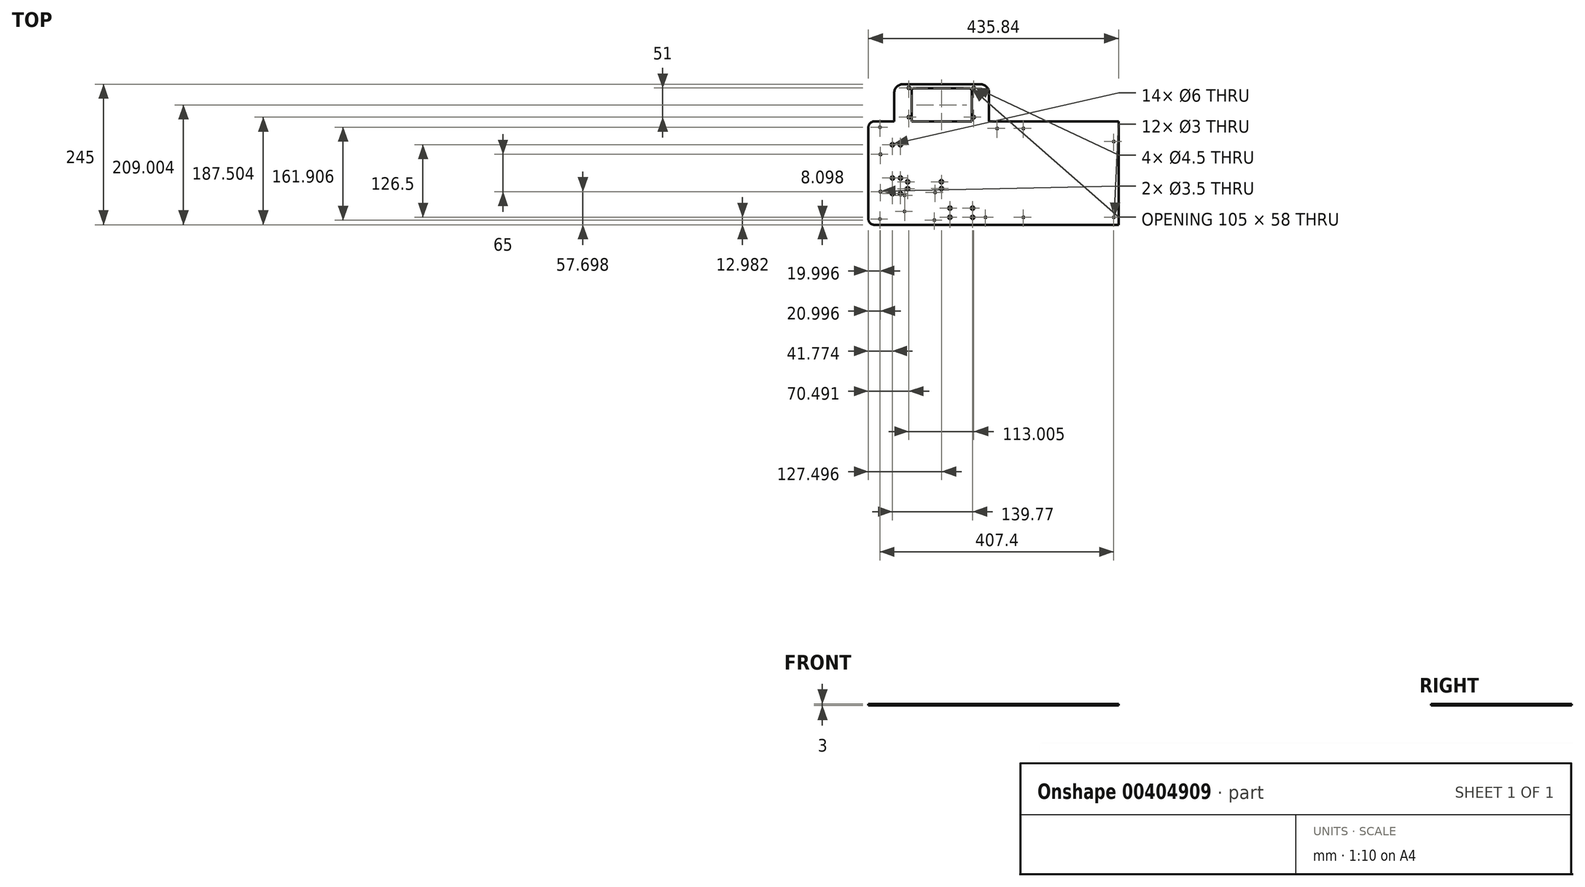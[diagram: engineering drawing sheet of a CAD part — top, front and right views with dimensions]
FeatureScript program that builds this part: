
annotation { "Feature Type Name" : "Feature", "Feature Type Description" : "" }
export const myFeature = defineFeature(function(context is Context, id is Id, definition is map)
    precondition{}
    {
        {
            var Q0;
            Q0=qCreatedBy(makeId("Top.planeOp"),FACE);
            var sketch = newSketch(context, id + "F0", { "sketchPlane" : qUnion([Q0])});
            skLineSegment(sketch, "E0.bottom", {"start": v(-167.12, 71.96) * mm, "end": v(268.72, 71.96) * mm});
            skLineSegment(sketch, "E0.top", {"start": v(-167.12, -108.04) * mm, "end": v(268.72, -108.04) * mm});
            skLineSegment(sketch, "E0.left", {"start": v(-167.12, 71.96) * mm, "end": v(-167.12, -108.04) * mm});
            skLineSegment(sketch, "E0.right", {"start": v(268.72, 71.96) * mm, "end": v(268.72, -108.04) * mm});
            skLineSegment(sketch, "E1.bottom", {"start": v(22.88, 69.96) * mm, "end": v(266.72, 69.96) * mm});
            skLineSegment(sketch, "E1.top", {"start": v(22.88, -103.04) * mm, "end": v(266.72, -103.04) * mm});
            skLineSegment(sketch, "E1.left", {"start": v(22.88, 69.96) * mm, "end": v(22.88, -103.04) * mm});
            skLineSegment(sketch, "E1.right", {"start": v(266.72, 69.96) * mm, "end": v(266.72, -103.04) * mm});
            skLineSegment(sketch, "E2", {"start": v(260.28, 69.96) * mm, "end": v(260.28, -103.04) * mm, "construction": true});
            skLineSegment(sketch, "E3", {"start": v(22.88, 59.8) * mm, "end": v(266.72, 59.8) * mm, "construction": true});
            skLineSegment(sketch, "E4", {"start": v(22.88, -95.04) * mm, "end": v(266.72, -95.04) * mm, "construction": true});
            skLineSegment(sketch, "E5", {"start": v(57.08, 69.96) * mm, "end": v(57.08, -103.04) * mm, "construction": true});
            skCircle(sketch, "E6", {"center": v(57.08, 59.8) * mm, "radius": 1.5 * mm});
            skCircle(sketch, "E7", {"center": v(102.8, 59.8) * mm, "radius": 1.5 * mm});
            skCircle(sketch, "E8", {"center": v(260.28, 36.95) * mm, "radius": 1.5 * mm});
            skCircle(sketch, "E9", {"center": v(260.28, -95.04) * mm, "radius": 1.5 * mm});
            skCircle(sketch, "E10", {"center": v(36.76, -95.04) * mm, "radius": 1.5 * mm});
            skCircle(sketch, "E11", {"center": v(102.8, -95.04) * mm, "radius": 1.5 * mm});
            skLineSegment(sketch, "E12.bottom", {"start": v(-106.12, 71.96) * mm, "end": v(20.88, 71.96) * mm});
            skLineSegment(sketch, "E12.top", {"start": v(-106.12, -30.04) * mm, "end": v(20.88, -30.04) * mm});
            skLineSegment(sketch, "E12.left", {"start": v(-106.12, 71.96) * mm, "end": v(-106.12, -30.04) * mm});
            skLineSegment(sketch, "E12.right", {"start": v(20.88, 71.96) * mm, "end": v(20.88, -30.04) * mm});
            skLineSegment(sketch, "E13.bottom", {"start": v(-161.12, 49.66) * mm, "end": v(-131.12, 49.66) * mm});
            skLineSegment(sketch, "E13.top", {"start": v(-161.12, -80.34) * mm, "end": v(-131.12, -80.34) * mm});
            skLineSegment(sketch, "E13.left", {"start": v(-161.12, 49.66) * mm, "end": v(-161.12, -80.34) * mm});
            skLineSegment(sketch, "E13.right", {"start": v(-131.12, 49.66) * mm, "end": v(-131.12, -80.34) * mm});
            skLineSegment(sketch, "E14.bottom", {"start": v(-35, -48.24) * mm, "end": v(-35, -103.54) * mm});
            skLineSegment(sketch, "E14.top", {"start": v(-106.6, -48.24) * mm, "end": v(-106.6, -103.54) * mm});
            skLineSegment(sketch, "E14.left", {"start": v(-35, -48.24) * mm, "end": v(-106.6, -48.24) * mm});
            skLineSegment(sketch, "E14.right", {"start": v(-35, -103.54) * mm, "end": v(-106.6, -103.54) * mm});
            skCircle(sketch, "E15", {"center": v(-51, -51.74) * mm, "radius": 1.5 * mm});
            skCircle(sketch, "E16", {"center": v(-52.3, -99.94) * mm, "radius": 1.5 * mm});
            skCircle(sketch, "E17", {"center": v(-104.1, -56.84) * mm, "radius": 1.5 * mm});
            skCircle(sketch, "E18", {"center": v(-104.1, -84.74) * mm, "radius": 1.5 * mm});
            skLineSegment(sketch, "E19", {"start": v(-146.12, 49.66) * mm, "end": v(-146.12, -80.34) * mm, "construction": true});
            skCircle(sketch, "E20", {"center": v(-146.12, 14.66) * mm, "radius": 1.75 * mm});
            skCircle(sketch, "E21", {"center": v(-146.12, -50.34) * mm, "radius": 1.75 * mm});
            skCircle(sketch, "E22", {"center": v(-147.12, 61.96) * mm, "radius": 1.5 * mm});
            skCircle(sketch, "E23", {"center": v(-147.12, -98.04) * mm, "radius": 1.5 * mm});
            skLineSegment(sketch, "E24.bottom", {"start": v(-106.12, 71.96) * mm, "end": v(42.88, 71.96) * mm});
            skLineSegment(sketch, "E24.top", {"start": v(-106.12, 136.96) * mm, "end": v(27.88, 136.96) * mm});
            skLineSegment(sketch, "E24.right", {"start": v(42.88, 71.96) * mm, "end": v(42.88, 121.96) * mm});
            skLineSegment(sketch, "E25.bottom", {"start": v(-84.64, 71.96) * mm, "end": v(13.47, 71.96) * mm});
            skLineSegment(sketch, "E25.top", {"start": v(-87.12, 129.96) * mm, "end": v(7.88, 129.96) * mm});
            skLineSegment(sketch, "E26", {"start": v(-92.12, 124.96) * mm, "end": v(-92.12, 71.96) * mm});
            skLineSegment(sketch, "E27", {"start": v(-92.12, 71.96) * mm, "end": v(12.88, 71.96) * mm});
            skLineSegment(sketch, "E28", {"start": v(12.88, 71.96) * mm, "end": v(12.88, 124.96) * mm});
            skLineSegment(sketch, "E29", {"start": v(-106.12, 136.96) * mm, "end": v(-107.12, 136.96) * mm});
            skLineSegment(sketch, "E30", {"start": v(-122.12, 121.96) * mm, "end": v(-122.12, 71.96) * mm});
            skPoint(sketch, "E31.visualSharp", {"position": v(-92.12, 129.96) * mm});
            skArc(sketch, "E31.filletArc", {"start": v(-87.12, 129.96) * mm, "mid": v(-90.66, 128.5) * mm, "end": v(-92.12, 124.96) * mm});
            skPoint(sketch, "E32.visualSharp", {"position": v(12.88, 129.96) * mm});
            skArc(sketch, "E32.filletArc", {"start": v(12.88, 124.96) * mm, "mid": v(11.41, 128.5) * mm, "end": v(7.88, 129.96) * mm});
            skPoint(sketch, "E33.visualSharp", {"position": v(-122.12, 136.96) * mm});
            skArc(sketch, "E33.filletArc", {"start": v(-107.12, 136.96) * mm, "mid": v(-117.73, 132.57) * mm, "end": v(-122.12, 121.96) * mm});
            skPoint(sketch, "E34.visualSharp", {"position": v(42.88, 136.96) * mm});
            skArc(sketch, "E34.filletArc", {"start": v(42.88, 121.96) * mm, "mid": v(38.48, 132.57) * mm, "end": v(27.88, 136.96) * mm});
            skCircle(sketch, "E35", {"center": v(16.38, 79.46) * mm, "radius": 2.25 * mm});
            skCircle(sketch, "E36", {"center": v(-96.62, 79.46) * mm, "radius": 2.25 * mm});
            skCircle(sketch, "E37", {"center": v(-96.63, 130.46) * mm, "radius": 2.25 * mm});
            skCircle(sketch, "E38", {"center": v(16.37, 130.46) * mm, "radius": 2.25 * mm});
            skLineSegment(sketch, "E39", {"start": v(16.37, 71.96) * mm, "end": v(16.37, 136.96) * mm, "construction": true});
            skCircle(sketch, "E40", {"center": v(-125.35, 31.44) * mm, "radius": 3 * mm});
            skCircle(sketch, "E41", {"center": v(-111.35, 31.42) * mm, "radius": 3 * mm});
            skCircle(sketch, "E42", {"center": v(-125.3, -26.6) * mm, "radius": 3 * mm});
            skCircle(sketch, "E43", {"center": v(-111.3, -26.61) * mm, "radius": 3 * mm});
            skCircle(sketch, "E44", {"center": v(-125.22, -53.77) * mm, "radius": 3 * mm});
            skCircle(sketch, "E45", {"center": v(-111.22, -53.79) * mm, "radius": 3 * mm});
            skCircle(sketch, "E46", {"center": v(-98.73, -33.12) * mm, "radius": 3 * mm});
            skCircle(sketch, "E47", {"center": v(-98.7, -45.12) * mm, "radius": 3 * mm});
            skCircle(sketch, "E48", {"center": v(-39.99, -33.03) * mm, "radius": 3 * mm});
            skCircle(sketch, "E49", {"center": v(-39.95, -45.03) * mm, "radius": 3 * mm});
            skCircle(sketch, "E50", {"center": v(14.39, -79.06) * mm, "radius": 3 * mm});
            skCircle(sketch, "E51", {"center": v(14.42, -95.06) * mm, "radius": 3 * mm});
            skCircle(sketch, "E52", {"center": v(-25.1, -79.02) * mm, "radius": 3 * mm});
            skCircle(sketch, "E53", {"center": v(-25.07, -95.02) * mm, "radius": 3 * mm});
            skSolve(sketch);
        }
        {
            var Q0;
            Q0=makeQuery(id+"F0.imprint","IMPRINT",FACE,{"disambiguationData":[TD([[makeQuery(id+"F0.imprint","IMPRINT",EDGE,{"derivedFrom":sQuery(id+"F0.wireOp",EDGE,"E24.top")}),-1.0]])]});
            var Q1;
            {var subQ2=sQuery(id+"F0.wireOp",EDGE,"E12.left");Q1=makeQuery(id+"F0.imprint","IMPRINT",FACE,{"disambiguationData":[TD([[makeQuery(id+"F0.imprint","IMPRINT",EDGE,{"derivedFrom":subQ2}),1.0]])]});}
            var Q2;
            Q2=makeQuery(id+"F0.imprint","IMPRINT",FACE,{"disambiguationData":[TD([[makeQuery(id+"F0.imprint","IMPRINT",EDGE,{"derivedFrom":sQuery(id+"F0.wireOp",EDGE,"E0.top")}),1.0]])]});
            var Q3;
            Q3=makeQuery(id+"F0.imprint","IMPRINT",FACE,{"disambiguationData":[TD([[makeQuery(id+"F0.imprint","IMPRINT",EDGE,{"derivedFrom":sQuery(id+"F0.wireOp",EDGE,"E13.bottom")}),-1.0]])]});
            var Q4;
            Q4=makeQuery(id+"F0.imprint","IMPRINT",FACE,{"disambiguationData":[TD([[makeQuery(id+"F0.imprint","IMPRINT",EDGE,{"derivedFrom":sQuery(id+"F0.wireOp",EDGE,"E14.bottom")}),-1.0]])]});
            var Q5;
            Q5=makeQuery(id+"F0.imprint","IMPRINT",FACE,{"disambiguationData":[TD([[makeQuery(id+"F0.imprint","IMPRINT",EDGE,{"derivedFrom":sQuery(id+"F0.wireOp",EDGE,"E1.bottom")}),-1.0]])]});
            extrude(context, id + "F1", {"entities" : qUnion([Q0, Q1, Q2, Q3, Q4, Q5]), "depth" : 3 * mm});
        }
        {
            var Q0;
            Q0=makeQuery(id+"F1.opExtrude","SWEPT_EDGE",EDGE,{"disambiguationData":[OSD([sQuery(id+"F0.wireOp",EDGE,"E0.bottom"),sQuery(id+"F0.wireOp",EDGE,"E0.left")])]});
            var Q1;
            Q1=makeQuery(id+"F1.opExtrude","SWEPT_EDGE",EDGE,{"disambiguationData":[OSD([sQuery(id+"F0.wireOp",EDGE,"E0.top"),sQuery(id+"F0.wireOp",EDGE,"E0.left")])]});
            fillet(context, id + "F2", {"entities" : qUnion([Q0, Q1]), "radius" : 10 * mm, "tangentPropagation" : true, "allowEdgeOverflow" : false});
        }
    });
